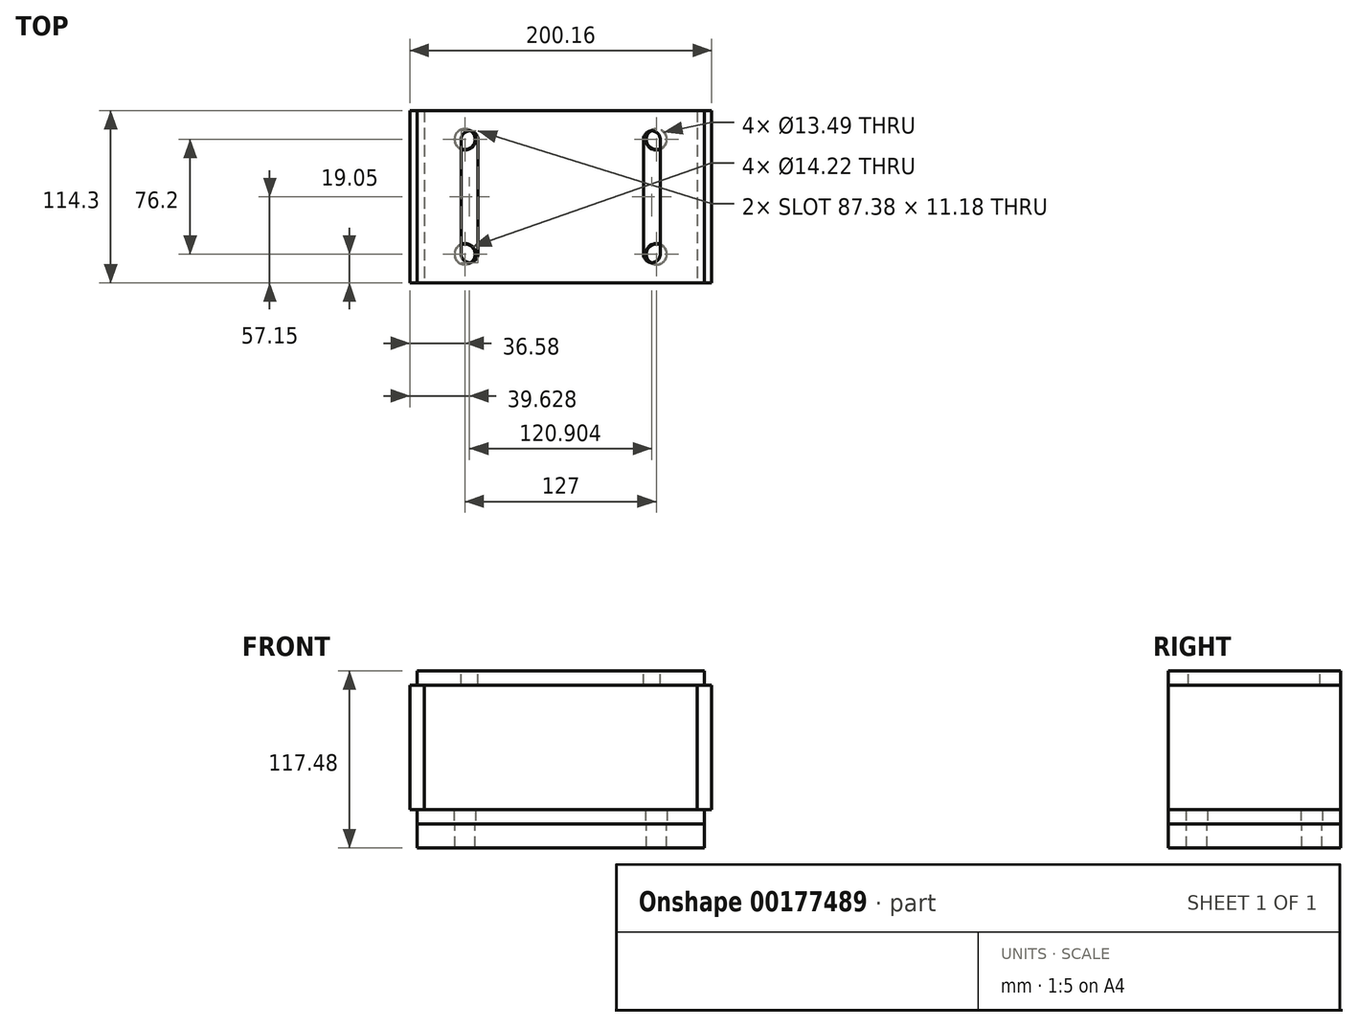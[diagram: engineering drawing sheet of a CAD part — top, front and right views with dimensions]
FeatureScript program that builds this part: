
annotation { "Feature Type Name" : "Feature", "Feature Type Description" : "" }
export const myFeature = defineFeature(function(context is Context, id is Id, definition is map)
    precondition{}
    {
        {
            var Q0;
            Q0=qCreatedBy(makeId("Top.planeOp"),FACE);
            var sketch = newSketch(context, id + "F0", { "sketchPlane" : qUnion([Q0])});
            skLineSegment(sketch, "E0.bottom", {"start": v(-95.25, 57.15) * mm, "end": v(95.25, 57.15) * mm});
            skLineSegment(sketch, "E0.top", {"start": v(-95.25, -57.15) * mm, "end": v(95.25, -57.15) * mm});
            skLineSegment(sketch, "E0.left", {"start": v(-95.25, 57.15) * mm, "end": v(-95.25, -57.15) * mm});
            skLineSegment(sketch, "E0.right", {"start": v(95.25, 57.15) * mm, "end": v(95.25, -57.15) * mm});
            skPoint(sketch, "E0.middle", {"position": v(0, 0) * mm});
            skLineSegment(sketch, "E1.bottom", {"start": v(-63.5, 38.1) * mm, "end": v(63.5, 38.1) * mm, "construction": true});
            skLineSegment(sketch, "E1.top", {"start": v(-63.5, -38.1) * mm, "end": v(63.5, -38.1) * mm, "construction": true});
            skLineSegment(sketch, "E1.left", {"start": v(-63.5, 38.1) * mm, "end": v(-63.5, -38.1) * mm, "construction": true});
            skLineSegment(sketch, "E1.right", {"start": v(63.5, 38.1) * mm, "end": v(63.5, -38.1) * mm, "construction": true});
            skCircle(sketch, "E2", {"center": v(-63.5, 38.1) * mm, "radius": 7.11 * mm});
            skCircle(sketch, "E3", {"center": v(63.5, 38.1) * mm, "radius": 7.11 * mm});
            skCircle(sketch, "E4", {"center": v(-63.5, -38.1) * mm, "radius": 7.11 * mm});
            skCircle(sketch, "E5", {"center": v(63.5, -38.1) * mm, "radius": 7.11 * mm});
            skSolve(sketch);
        }
        {
            var Q0;
            Q0 = qSketchRegion(id + "F0", true);
            extrude(context, id + "F1", {"entities" : qUnion([Q0]), "depth" : 9.65 * mm});
        }
        {
            var Q0;
            Q0=qCreatedBy(makeId("Top.planeOp"),FACE);
            cPlane(context, id + "F2", {"entities" : qUnion([Q0]), "cplaneType" : CPlaneType.OFFSET, "offset" : 101.6 * mm, "width" : 152.4 * mm, "height" : 152.4 * mm});
        }
        {
            var Q0;
            Q0=qCreatedBy(id+"F2.planeOp",FACE);
            var sketch = newSketch(context, id + "F3", { "sketchPlane" : qUnion([Q0])});
            skLineSegment(sketch, "E6.bottom", {"start": v(-95.25, 57.15) * mm, "end": v(95.25, 57.15) * mm});
            skLineSegment(sketch, "E6.top", {"start": v(-95.25, -57.15) * mm, "end": v(95.25, -57.15) * mm});
            skLineSegment(sketch, "E6.left", {"start": v(-95.25, 57.15) * mm, "end": v(-95.25, -57.15) * mm});
            skLineSegment(sketch, "E6.right", {"start": v(95.25, 57.15) * mm, "end": v(95.25, -57.15) * mm});
            skPoint(sketch, "E6.middle", {"position": v(0, 0) * mm});
            skLineSegment(sketch, "E7", {"start": v(0, 57.15) * mm, "end": v(0, -57.15) * mm, "construction": true});
            skLineSegment(sketch, "E8.0", {"start": v(-60.45, 38.1) * mm, "end": v(-60.45, -38.1) * mm, "construction": true});
            skLineSegment(sketch, "E9", {"start": v(0, 0) * mm, "end": v(-130.21, 0) * mm, "construction": true});
            skLineSegment(sketch, "E10.0", {"start": v(0, 38.1) * mm, "end": v(-130.21, 38.1) * mm, "construction": true});
            skLineSegment(sketch, "E11.MirrorCS", {"start": v(0, -38.1) * mm, "end": v(-130.21, -38.1) * mm, "construction": true});
            skArc(sketch, "E12.0.startCap", {"start": v(-66.04, 38.1) * mm, "mid": v(-60.45, 43.69) * mm, "end": v(-54.86, 38.1) * mm});
            skArc(sketch, "E12.0.endCap", {"start": v(-54.86, -38.1) * mm, "mid": v(-60.45, -43.69) * mm, "end": v(-66.04, -38.1) * mm});
            skLineSegment(sketch, "E12.0.left", {"start": v(-54.86, 38.1) * mm, "end": v(-54.86, -38.1) * mm});
            skLineSegment(sketch, "E12.0.right", {"start": v(-66.04, 38.1) * mm, "end": v(-66.04, -38.1) * mm});
            skLineSegment(sketch, "E13.MirrorCS", {"start": v(66.04, 38.1) * mm, "end": v(66.04, -38.1) * mm});
            skLineSegment(sketch, "E14.MirrorCS", {"start": v(54.86, 38.1) * mm, "end": v(54.86, -38.1) * mm});
            skArc(sketch, "E15.MirrorCS", {"start": v(54.86, -38.1) * mm, "mid": v(60.45, -43.69) * mm, "end": v(66.04, -38.1) * mm});
            skArc(sketch, "E16.MirrorCS", {"start": v(66.04, 38.1) * mm, "mid": v(60.45, 43.69) * mm, "end": v(54.86, 38.1) * mm});
            skLineSegment(sketch, "E17.MirrorCS", {"start": v(60.45, 38.1) * mm, "end": v(60.45, -38.1) * mm, "construction": true});
            skSolve(sketch);
        }
        {
            var Q0;
            Q0 = qSketchRegion(id + "F3", true);
            extrude(context, id + "F4", {"entities" : qUnion([Q0]), "oppositeDirection" : true, "depth" : 9.65 * mm});
        }
        {
            var Q0;
            Q0=makeQuery(id+"F1.opExtrude","SWEPT_FACE",FACE,{"disambiguationData":[OSD([sQuery(id+"F0.wireOp",EDGE,"E0.left")])]});
            var sketch = newSketch(context, id + "F5", { "sketchPlane" : qUnion([Q0])});
            skLineSegment(sketch, "E18.0", {"start": v(-57.15, 9.65) * mm, "end": v(57.15, 9.65) * mm});
            skLineSegment(sketch, "E19.0", {"start": v(-57.15, 91.95) * mm, "end": v(57.15, 91.95) * mm});
            skLineSegment(sketch, "E20", {"start": v(-57.15, 9.65) * mm, "end": v(-57.15, 91.95) * mm});
            skLineSegment(sketch, "E21", {"start": v(57.15, 9.65) * mm, "end": v(57.15, 91.95) * mm});
            skSolve(sketch);
        }
        {
            var Q0;
            Q0 = qSketchRegion(id + "F5", true);
            extrude(context, id + "F6", {"entities" : qUnion([Q0]), "endBound" : BoundingType.SYMMETRIC, "depth" : 9.65 * mm});
        }
        {
            var Q0;
            Q0=makeQuery(id+"F6.opExtrude","SWEPT_BODY",BODY,{"disambiguationData":[OSD([sQuery(id+"F5.wireOp",EDGE,"E18.0"),sQuery(id+"F5.wireOp",EDGE,"E19.0"),sQuery(id+"F5.wireOp",EDGE,"E20"),sQuery(id+"F5.wireOp",EDGE,"E21")])]});
            var Q1;
            Q1=qCreatedBy(makeId("Right.planeOp"),FACE);
            mirror(context, id + "F7", {"entities" : qUnion([Q0]), "mirrorPlane" : qUnion([Q1])});
        }
        {
            var Q0;
            Q0=makeQuery(id+"F1.opExtrude","CAP_FACE",FACE,{"disambiguationData":[OSD([sQuery(id+"F0.wireOp",EDGE,"E0.bottom"),sQuery(id+"F0.wireOp",EDGE,"E0.top"),sQuery(id+"F0.wireOp",EDGE,"E0.left"),sQuery(id+"F0.wireOp",EDGE,"E0.right"),sQuery(id+"F0.wireOp",EDGE,"E2"),sQuery(id+"F0.wireOp",EDGE,"E3"),sQuery(id+"F0.wireOp",EDGE,"E4"),sQuery(id+"F0.wireOp",EDGE,"E5")])],"isStart":true});
            var sketch = newSketch(context, id + "F8", { "sketchPlane" : qUnion([Q0])});
            skLineSegment(sketch, "E22.0.0", {"start": v(-95.25, -57.15) * mm, "end": v(95.25, -57.15) * mm});
            skLineSegment(sketch, "E22.0.1", {"start": v(95.25, -57.15) * mm, "end": v(95.25, 57.15) * mm});
            skLineSegment(sketch, "E22.0.2", {"start": v(95.25, 57.15) * mm, "end": v(-95.25, 57.15) * mm});
            skLineSegment(sketch, "E22.0.3", {"start": v(-95.25, 57.15) * mm, "end": v(-95.25, -57.15) * mm});
            skCircle(sketch, "E23.0", {"center": v(-63.5, 38.1) * mm, "radius": 7.11 * mm, "construction": true});
            skCircle(sketch, "E24.0", {"center": v(-63.5, -38.1) * mm, "radius": 7.11 * mm, "construction": true});
            skCircle(sketch, "E25.0", {"center": v(63.5, 38.1) * mm, "radius": 7.11 * mm, "construction": true});
            skCircle(sketch, "E26.0", {"center": v(63.5, -38.1) * mm, "radius": 7.11 * mm, "construction": true});
            skSolve(sketch);
        }
        {
            var Q0;
            Q0 = qSketchRegion(id + "F8", true);
            extrude(context, id + "F9", {"entities" : qUnion([Q0]), "depth" : 15.88 * mm});
        }
        {
            var Q0;
            Q0=sQuery(id+"F8.wireOp",VERTEX,"E24.0.center");
            var Q1;
            Q1=sQuery(id+"F8.wireOp",VERTEX,"E26.0.center");
            var Q2;
            Q2=sQuery(id+"F8.wireOp",VERTEX,"E25.0.center");
            var Q3;
            Q3=sQuery(id+"F8.wireOp",VERTEX,"E23.0.center");
            var Q4;
            Q4=makeQuery(id+"F9.opExtrude","SWEPT_BODY",BODY,{"disambiguationData":[OSD([sQuery(id+"F8.wireOp",EDGE,"E22.0.0"),sQuery(id+"F8.wireOp",EDGE,"E22.0.1"),sQuery(id+"F8.wireOp",EDGE,"E22.0.2"),sQuery(id+"F8.wireOp",EDGE,"E22.0.3")])]});
            hole(context, id + "F10", {"style" : HoleStyle.SIMPLE, "endStyle" : HoleEndStyle.THROUGH, "oppositeDirection" : true, "standardTappedOrClearance" : lookupTablePath({ "standard" : "ANSI", "fit" : "Normal (ASME)", "size" : "1/2", "type" : "Clearance" }), "standardBlindInLast" : lookupTablePath({ "fit" : "Free", "standard" : "ANSI", "size" : "1/2", "type" : "Clearance" }), "holeDiameter" : 13.5 * mm, "locations" : qUnion([Q0, Q1, Q2, Q3]), "scope" : qUnion([Q4]), "isTappedThrough" : true});
        }
    });
